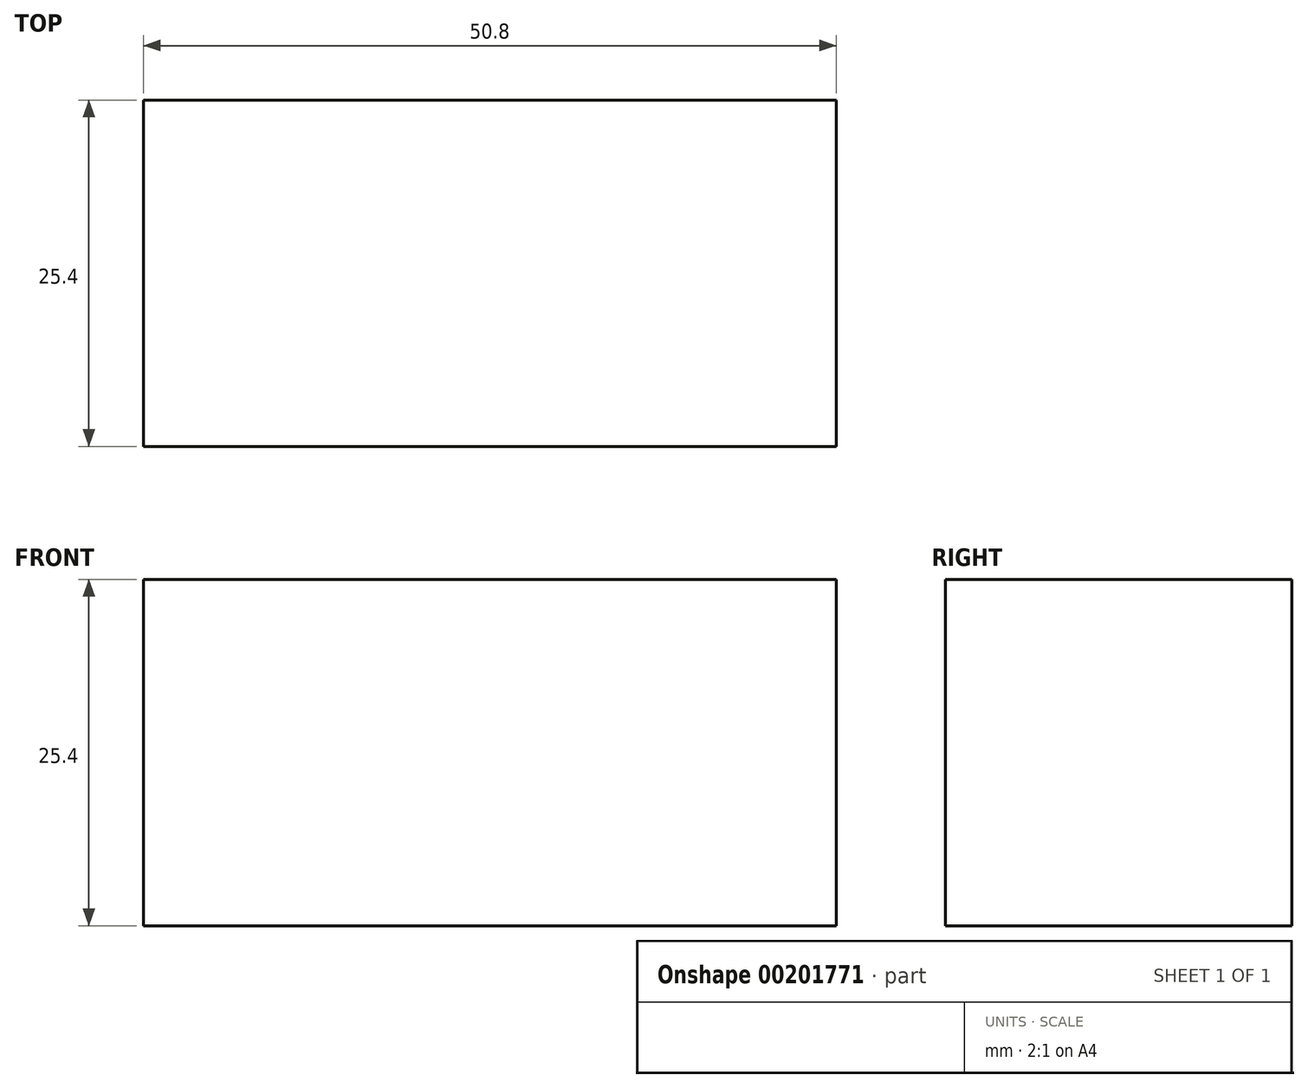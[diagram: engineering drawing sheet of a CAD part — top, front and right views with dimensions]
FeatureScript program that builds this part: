
annotation { "Feature Type Name" : "Feature", "Feature Type Description" : "" }
export const myFeature = defineFeature(function(context is Context, id is Id, definition is map)
    precondition{}
    {
        {
            var Q0;
            Q0=qCreatedBy(makeId("Front.planeOp"),FACE);
            var sketch = newSketch(context, id + "F0", { "sketchPlane" : qUnion([Q0])});
            skLineSegment(sketch, "E0.bottom", {"start": v(25.4, 12.7) * mm, "end": v(-25.4, 12.7) * mm});
            skLineSegment(sketch, "E0.top", {"start": v(25.4, -12.7) * mm, "end": v(-25.4, -12.7) * mm});
            skLineSegment(sketch, "E0.left", {"start": v(25.4, 12.7) * mm, "end": v(25.4, -12.7) * mm});
            skLineSegment(sketch, "E0.right", {"start": v(-25.4, 12.7) * mm, "end": v(-25.4, -12.7) * mm});
            skPoint(sketch, "E0.middle", {"position": v(0, 0) * mm});
            skSolve(sketch);
        }
        {
            var Q0;
            Q0 = qSketchRegion(id + "F0", true);
            extrude(context, id + "F1", {"entities" : qUnion([Q0]), "depth" : 25.4 * mm});
        }
    });
